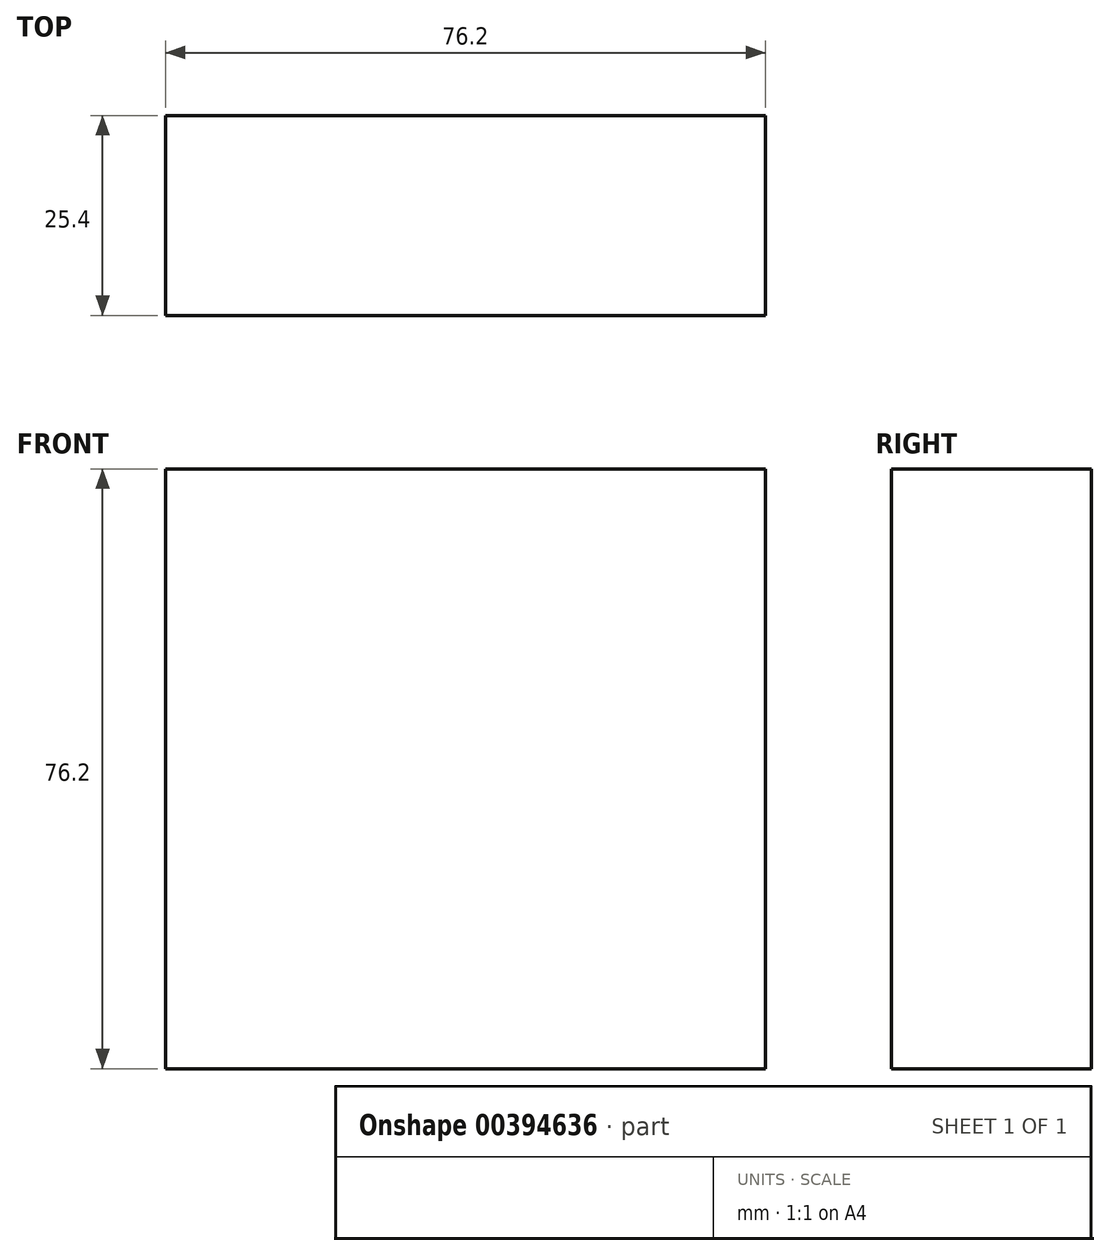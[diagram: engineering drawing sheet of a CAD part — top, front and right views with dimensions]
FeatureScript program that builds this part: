
annotation { "Feature Type Name" : "Feature", "Feature Type Description" : "" }
export const myFeature = defineFeature(function(context is Context, id is Id, definition is map)
    precondition{}
    {
        {
            var Q0;
            Q0=qCreatedBy(makeId("Front.planeOp"),FACE);
            var sketch = newSketch(context, id + "F0", { "sketchPlane" : qUnion([Q0])});
            skLineSegment(sketch, "E0.bottom", {"start": v(-30.61, -16.97) * mm, "end": v(45.59, -16.97) * mm});
            skLineSegment(sketch, "E0.top", {"start": v(-30.61, 59.23) * mm, "end": v(45.59, 59.23) * mm});
            skLineSegment(sketch, "E0.left", {"start": v(-30.61, -16.97) * mm, "end": v(-30.61, 59.23) * mm});
            skLineSegment(sketch, "E0.right", {"start": v(45.59, -16.97) * mm, "end": v(45.59, 59.23) * mm});
            skLineSegment(sketch, "E1.bottom", {"start": v(-18.4, -8.53) * mm, "end": v(32.4, -8.53) * mm});
            skLineSegment(sketch, "E1.top", {"start": v(-18.4, 16.87) * mm, "end": v(32.4, 16.87) * mm});
            skLineSegment(sketch, "E1.left", {"start": v(-18.4, -8.53) * mm, "end": v(-18.4, 16.87) * mm});
            skLineSegment(sketch, "E1.right", {"start": v(32.4, -8.53) * mm, "end": v(32.4, 16.87) * mm});
            skSolve(sketch);
        }
        {
            var Q0;
            Q0=makeQuery(id+"F0.imprint","IMPRINT",FACE,{"disambiguationData":[TD([[makeQuery(id+"F0.imprint","IMPRINT",EDGE,{"derivedFrom":sQuery(id+"F0.wireOp",EDGE,"E0.bottom")}),1.0]])]});
            var Q1;
            Q1=makeQuery(id+"F0.imprint","IMPRINT",FACE,{"disambiguationData":[TD([[makeQuery(id+"F0.imprint","IMPRINT",EDGE,{"derivedFrom":sQuery(id+"F0.wireOp",EDGE,"E1.bottom")}),1.0]])]});
            extrude(context, id + "F1", {"entities" : qUnion([Q0, Q1]), "depth" : 25.4 * mm});
        }
    });
